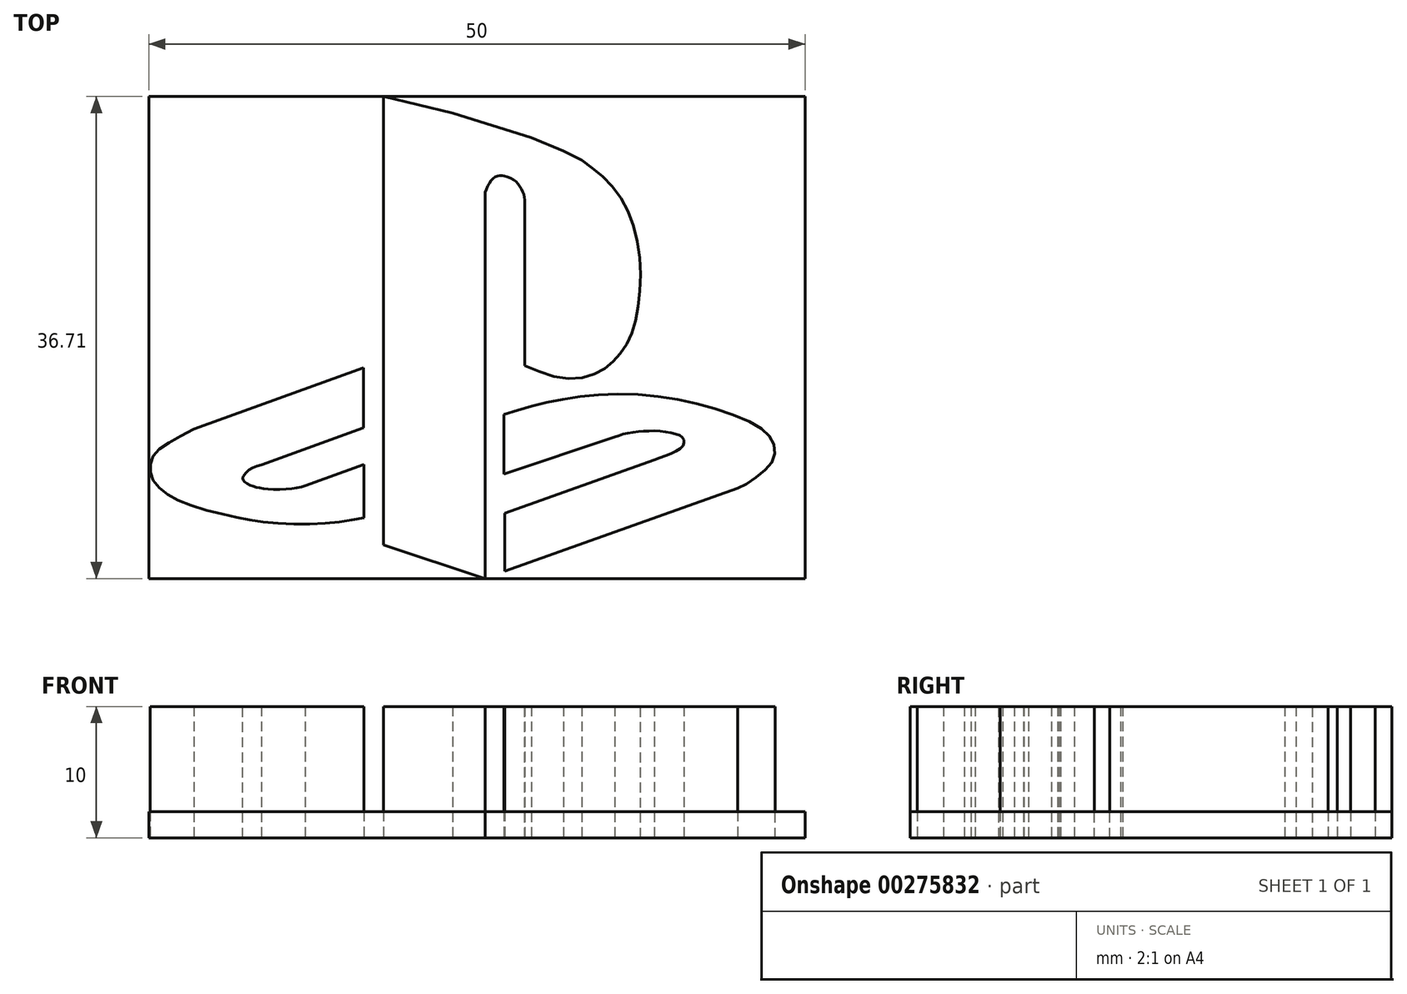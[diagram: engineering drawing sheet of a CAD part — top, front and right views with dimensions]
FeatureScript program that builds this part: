
annotation { "Feature Type Name" : "Feature", "Feature Type Description" : "" }
export const myFeature = defineFeature(function(context is Context, id is Id, definition is map)
    precondition{}
    {
        {
            var Q0;
            Q0=qCreatedBy(makeId("Top.planeOp"),FACE);
            var sketch = newSketch(context, id + "F0", { "sketchPlane" : qUnion([Q0])});
            skLineSegment(sketch, "E0", {"start": v(17.9, 36.7) * mm, "end": v(17.9, 2.56) * mm});
            skLineSegment(sketch, "E1", {"start": v(17.9, 2.56) * mm, "end": v(25.63, 0) * mm});
            skLineSegment(sketch, "E2", {"start": v(25.63, 0) * mm, "end": v(25.63, 29.42) * mm});
            skLineSegment(sketch, "E3", {"start": v(17.9, 36.7) * mm, "end": v(23.15, 35.44) * mm});
            skLineSegment(sketch, "E4", {"start": v(23.15, 35.44) * mm, "end": v(29.17, 33.56) * mm});
            skLineSegment(sketch, "E5", {"start": v(29.17, 33.56) * mm, "end": v(31.6, 32.57) * mm});
            skLineSegment(sketch, "E6", {"start": v(31.6, 32.57) * mm, "end": v(32.98, 31.85) * mm});
            skFitSpline(sketch, "E7", {"points": [v(32.98, 31.85) * mm, v(34.96, 30.27) * mm, v(36.6, 27.77) * mm, v(37.41, 24.25) * mm, v(37.27, 20.54) * mm, v(36.6, 18.18) * mm, v(35.53, 16.69) * mm, v(34.19, 15.67) * mm, v(31.78, 15.24) * mm, v(28.64, 16.2) * mm], "startDerivative": vector(19.03, -13.24) * mm, "endDerivative": vector(-25.75, 10.74) * mm});
            skLineSegment(sketch, "E8", {"start": v(28.64, 16.2) * mm, "end": v(28.64, 28.55) * mm});
            skFitSpline(sketch, "E9", {"points": [v(28.64, 28.55) * mm, v(28.64, 28.94) * mm, v(28.4, 29.65) * mm, v(27.88, 30.3) * mm, v(27.07, 30.67) * mm, v(26.59, 30.67) * mm, v(26.05, 30.26) * mm, v(25.63, 29.42) * mm], "startDerivative": vector(0.3, 3.39) * mm, "endDerivative": vector(-2.09, -5.5) * mm});
            skLineSegment(sketch, "E10", {"start": v(27.08, 12.51) * mm, "end": v(27.08, 7.96) * mm});
            skLineSegment(sketch, "E11", {"start": v(27.12, 4.98) * mm, "end": v(27.12, 0.55) * mm});
            skLineSegment(sketch, "E12", {"start": v(27.12, 0.55) * mm, "end": v(44.87, 6.87) * mm});
            skLineSegment(sketch, "E13", {"start": v(27.12, 4.98) * mm, "end": v(38.51, 9.05) * mm});
            skLineSegment(sketch, "E14", {"start": v(27.08, 7.96) * mm, "end": v(35.5, 10.78) * mm});
            skLineSegment(sketch, "E15", {"start": v(16.36, 16.05) * mm, "end": v(16.36, 11.46) * mm});
            skLineSegment(sketch, "E16", {"start": v(16.36, 11.46) * mm, "end": v(8.6, 8.65) * mm});
            skLineSegment(sketch, "E17", {"start": v(16.36, 16.05) * mm, "end": v(3.44, 11.38) * mm});
            skLineSegment(sketch, "E18", {"start": v(16.38, 8.68) * mm, "end": v(16.38, 4.64) * mm});
            skLineSegment(sketch, "E19", {"start": v(16.38, 8.68) * mm, "end": v(11.92, 7.07) * mm});
            skFitSpline(sketch, "E20", {"points": [v(8.6, 8.65) * mm, v(7.67, 8.3) * mm, v(7.27, 7.9) * mm, v(7.21, 7.8) * mm, v(7.16, 7.68) * mm, v(7.19, 7.5) * mm, v(7.45, 7.24) * mm, v(7.92, 7.03) * mm, v(8.4, 6.9) * mm, v(9.34, 6.8) * mm, v(11.02, 6.86) * mm, v(11.92, 7.07) * mm], "startDerivative": vector(-8.21, -2.22) * mm, "endDerivative": vector(6.76, 1.96) * mm});
            skFitSpline(sketch, "E21", {"points": [v(3.44, 11.38) * mm, v(1.22, 10.14) * mm, v(0.33, 9.31) * mm, v(0.12, 8.42) * mm, v(0.28, 7.56) * mm, v(1.14, 6.6) * mm, v(2.82, 5.7) * mm, v(6.04, 4.8) * mm, v(8.35, 4.36) * mm, v(11.4, 4.13) * mm, v(14.35, 4.3) * mm, v(16.38, 4.64) * mm], "startDerivative": vector(-23.5, -12.32) * mm, "endDerivative": vector(20.72, 4) * mm});
            skFitSpline(sketch, "E22", {"points": [v(35.5, 10.78) * mm, v(36.34, 11.04) * mm, v(37.5, 11.2) * mm, v(38.75, 11.24) * mm, v(40, 11.04) * mm, v(40.63, 10.78) * mm, v(40.78, 10.46) * mm, v(40.7, 10.12) * mm, v(39.9, 9.56) * mm, v(38.51, 9.05) * mm], "startDerivative": vector(7.3, 2.6) * mm, "endDerivative": vector(-9.94, -3.2) * mm});
            skFitSpline(sketch, "E23", {"points": [v(27.08, 12.51) * mm, v(29.17, 13.12) * mm, v(31.76, 13.7) * mm, v(35.26, 14.03) * mm, v(39.48, 13.78) * mm, v(43.25, 12.89) * mm, v(46.28, 11.68) * mm, v(47.33, 10.78) * mm, v(47.7, 9.96) * mm, v(47.6, 9.05) * mm, v(46.99, 8.29) * mm, v(45.82, 7.37) * mm, v(44.87, 6.87) * mm], "startDerivative": vector(23.83, 7.17) * mm, "endDerivative": vector(-15.2, -7.05) * mm});
            skSolve(sketch);
        }
        {
            var Q0;
            Q0 = qSketchRegion(id + "F0", true);
            extrude(context, id + "F1", {"entities" : qUnion([Q0]), "depth" : 10 * mm});
        }
        {
            var Q0;
            Q0=qCreatedBy(makeId("Top.planeOp"),FACE);
            var sketch = newSketch(context, id + "F2", { "sketchPlane" : qUnion([Q0])});
            skLineSegment(sketch, "E24.bottom", {"start": v(0, 36.7) * mm, "end": v(50, 36.7) * mm});
            skLineSegment(sketch, "E24.top", {"start": v(0, 0) * mm, "end": v(50, 0) * mm});
            skLineSegment(sketch, "E24.left", {"start": v(0, 36.7) * mm, "end": v(0, 0) * mm});
            skLineSegment(sketch, "E24.right", {"start": v(50, 36.7) * mm, "end": v(50, 0) * mm});
            skSolve(sketch);
        }
        {
            var Q0;
            Q0=makeQuery(id+"F2.imprint","IMPRINT",FACE,{"disambiguationData":[TD([[makeQuery(id+"F2.imprint","IMPRINT",EDGE,{"derivedFrom":sQuery(id+"F2.wireOp",EDGE,"E24.bottom")}),-1.0]])]});
            extrude(context, id + "F3", {"entities" : qUnion([Q0]), "depth" : 2 * mm});
        }
    });
